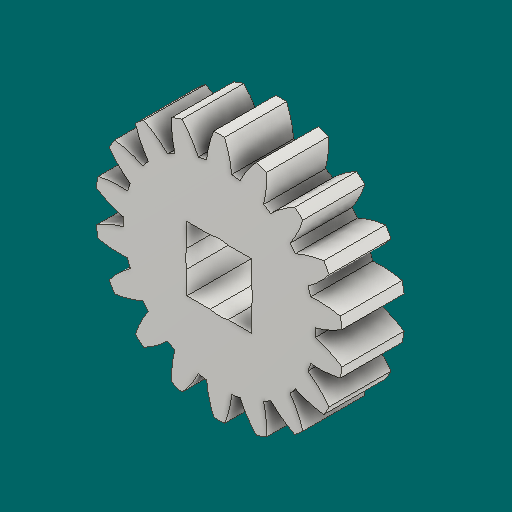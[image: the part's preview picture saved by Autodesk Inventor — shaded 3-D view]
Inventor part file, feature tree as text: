
AUTODESK INVENTOR PART (.ipt)
format: ipt  version: 2023.1 (Build 271208000, 208)  size: 321,536 bytes
history: native  units: in
note: dims shown in document units (in); Inventor stores cm internally (conversion verified against a paired STEP export)
features: other x12, sketch x4, plane x3
ambient origin geometry x8: Origin, YZ Plane, XZ Plane, XY Plane, X Axis, Y Axis, Z Axis, Center Point
bodies: Solid1 (feature_tree)
feature tree (19):
  other  "Spur Gear11_MIR.ipt"
  other  "Solid1::Spur Gear11_MIR.ipt"
  other  "TaggingFeature1"
  sketch  "Sketch1"  dims[d0=0.3937in]
  sketch  "Sketch2"  dims[d9=0.0in]
  sketch  "Sketch3"  dims[d14=0.0in]
  sketch  "Sketch4"  dims[d15=0.9in d16=0.0in d17=0.0in d18=0.0in d19=0.9in]
  plane  "XZ Plane_1"
  plane  "Work Plane2"
  plane  "Work Plane3"
  other  "Srf1"
  other  "Srf1::Derived"
  other  "Start plane iMate"
  other  "Distance iMate"
  other  "Position iMate"
  other  "Mesh iMate"
  other  "Axis iMate"
  other  "Mesh iMate2"
  other  "Align iMate"
